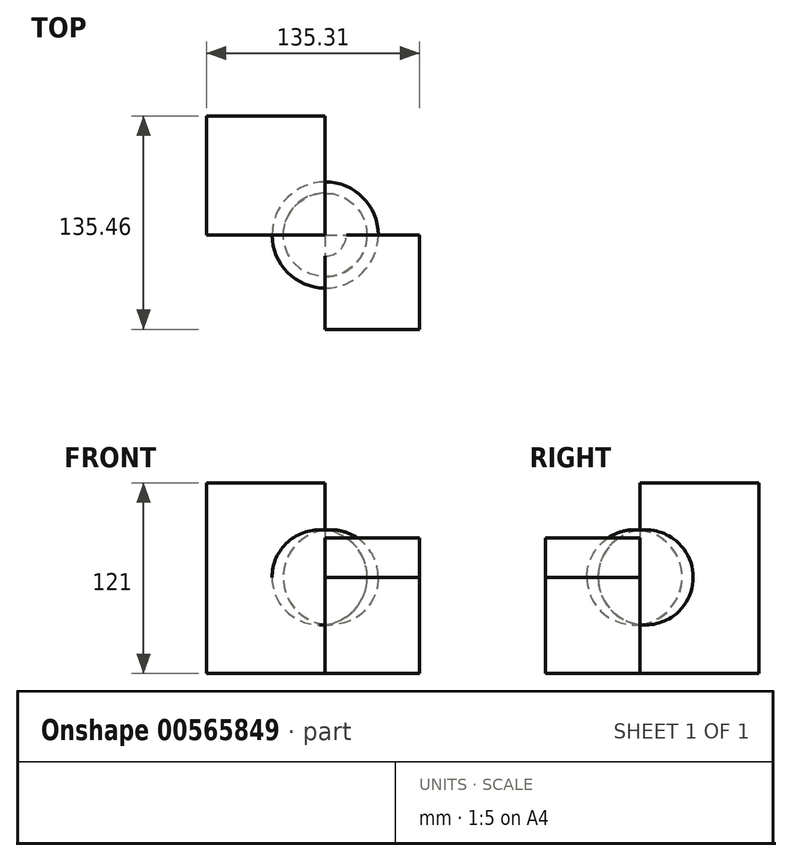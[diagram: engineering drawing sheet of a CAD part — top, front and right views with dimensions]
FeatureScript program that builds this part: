
annotation { "Feature Type Name" : "Feature", "Feature Type Description" : "" }
export const myFeature = defineFeature(function(context is Context, id is Id, definition is map)
    precondition{}
    {
        {
            var Q0;
            Q0=qCreatedBy(makeId("Front.planeOp"),FACE);
            var sketch = newSketch(context, id + "F0", { "sketchPlane" : qUnion([Q0])});
            skLineSegment(sketch, "E0", {"start": v(0, -30) * mm, "end": v(0, 30) * mm});
            skLineSegment(sketch, "E1", {"start": v(0, 0) * mm, "end": v(72.13, 0) * mm, "construction": true});
            skArc(sketch, "E2", {"start": v(0, 30) * mm, "mid": v(-26.67, 0) * mm, "end": v(0, -30) * mm});
            skSolve(sketch);
        }
        {
            var Q0;
            Q0=makeQuery(id+"F0.imprint","IMPRINT",FACE,{"disambiguationData":[TD([[makeQuery(id+"F0.imprint","IMPRINT",EDGE,{"derivedFrom":sQuery(id+"F0.wireOp",EDGE,"E0")}),1.0]])]});
            var Q1;
            Q1=sQuery(id+"F0.wireOp",EDGE,"E0");
            revolve(context, id + "F1", {"entities" : qUnion([Q0]), "axis" : qUnion([Q1]), "revolveType" : RevolveType.FULL});
        }
        {
            var Q0;
            Q0=qCreatedBy(makeId("Top.planeOp"),FACE);
            var sketch = newSketch(context, id + "F2", { "sketchPlane" : qUnion([Q0])});
            skLineSegment(sketch, "E3.bottom", {"start": v(0, 0) * mm, "end": v(60, 0) * mm});
            skLineSegment(sketch, "E3.top", {"start": v(0, -60) * mm, "end": v(60, -60) * mm});
            skLineSegment(sketch, "E3.right", {"start": v(60, 0) * mm, "end": v(60, -60) * mm});
            skLineSegment(sketch, "E4", {"start": v(0, 0) * mm, "end": v(0, -60) * mm});
            skPoint(sketch, "E3.left.end.orphan", {"position": v(-60, -60) * mm});
            skPoint(sketch, "E5.orphan", {"position": v(-60, 0) * mm});
            skLineSegment(sketch, "E6", {"start": v(0, 0) * mm, "end": v(0, 52.1) * mm, "construction": true});
            skSolve(sketch);
        }
        {
            var Q0;
            Q0 = qSketchRegion(id + "F2", true);
            extrude(context, id + "F3", {"entities" : qUnion([Q0]), "depth" : 25 * mm, "offsetDistance" : 25 * mm});
        }
        {
            var Q0;
            Q0=makeQuery(id+"F1.opRevolve","SWEPT_BODY",BODY,{"disambiguationData":[OSD([sQuery(id+"F0.wireOp",EDGE,"E0"),sQuery(id+"F0.wireOp",EDGE,"E2")])]});
            var Q1;
            Q1=makeQuery(id+"F3.opExtrude","SWEPT_BODY",BODY,{"disambiguationData":[OSD([sQuery(id+"F2.wireOp",EDGE,"E3.bottom"),sQuery(id+"F2.wireOp",EDGE,"E3.top"),sQuery(id+"F2.wireOp",EDGE,"E3.right"),sQuery(id+"F2.wireOp",EDGE,"E4")])]});
            booleanBodies(context, id + "F4", {"operationType" : BooleanOperationType.SUBTRACTION, "tools" : qUnion([Q0]), "targets" : qUnion([Q1]), "keepTools" : true});
        }
        {
            var Q0;
            Q0=makeQuery(id+"F3.opExtrude","CAP_FACE",FACE,{"disambiguationData":[OSD([sQuery(id+"F2.wireOp",EDGE,"E3.bottom"),sQuery(id+"F2.wireOp",EDGE,"E3.top"),sQuery(id+"F2.wireOp",EDGE,"E3.right"),sQuery(id+"F2.wireOp",EDGE,"E4")])],"isStart":true});
            var sketch = newSketch(context, id + "F5", { "sketchPlane" : qUnion([Q0])});
            skLineSegment(sketch, "E7.bottom", {"start": v(60, 60) * mm, "end": v(0, 60) * mm});
            skLineSegment(sketch, "E7.top", {"start": v(60, 0) * mm, "end": v(0, 0) * mm});
            skLineSegment(sketch, "E7.left", {"start": v(60, 60) * mm, "end": v(60, 0) * mm});
            skLineSegment(sketch, "E7.right", {"start": v(0, 60) * mm, "end": v(0, 0) * mm});
            skSolve(sketch);
        }
        {
            var Q0;
            Q0 = qSketchRegion(id + "F5", true);
            extrude(context, id + "F6", {"entities" : qUnion([Q0]), "depth" : 61 * mm, "offsetDistance" : 25 * mm});
        }
        {
            var Q0;
            Q0=makeQuery(id+"F6.opExtrude","CAP_FACE",FACE,{"disambiguationData":[OSD([sQuery(id+"F5.wireOp",EDGE,"E7.bottom"),sQuery(id+"F5.wireOp",EDGE,"E7.top"),sQuery(id+"F5.wireOp",EDGE,"E7.left"),sQuery(id+"F5.wireOp",EDGE,"E7.right")])],"isStart":false});
            var sketch = newSketch(context, id + "F7", { "sketchPlane" : qUnion([Q0])});
            skLineSegment(sketch, "E8.bottom", {"start": v(0, 0) * mm, "end": v(-75.3, 0) * mm});
            skLineSegment(sketch, "E8.top", {"start": v(0, -75.46) * mm, "end": v(-75.3, -75.46) * mm});
            skLineSegment(sketch, "E8.left", {"start": v(0, 0) * mm, "end": v(0, -75.46) * mm});
            skLineSegment(sketch, "E8.right", {"start": v(-75.3, 0) * mm, "end": v(-75.3, -75.46) * mm});
            skSolve(sketch);
        }
        {
            var Q0;
            Q0=makeQuery(id+"F7.imprint","IMPRINT",FACE,{"disambiguationData":[TD([[makeQuery(id+"F7.imprint","IMPRINT",EDGE,{"derivedFrom":sQuery(id+"F7.wireOp",EDGE,"E8.bottom")}),1.0]])]});
            extrude(context, id + "F8", {"entities" : qUnion([Q0]), "flatOperationType" : FlatOperationType.REMOVE, "oppositeDirection" : true, "depth" : 121 * mm, "offsetDistance" : 25 * mm, "domain" : OperationDomain.MODEL});
        }
        {
            var Q0;
            Q0=makeQuery(id+"F1.opRevolve","SWEPT_BODY",BODY,{"disambiguationData":[OSD([sQuery(id+"F0.wireOp",EDGE,"E0"),sQuery(id+"F0.wireOp",EDGE,"E2")])]});
            var Q1;
            Q1=makeQuery(id+"F8.opExtrude","SWEPT_BODY",BODY,{"disambiguationData":[OSD([sQuery(id+"F7.wireOp",EDGE,"E8.bottom"),sQuery(id+"F7.wireOp",EDGE,"E8.top"),sQuery(id+"F7.wireOp",EDGE,"E8.left"),sQuery(id+"F7.wireOp",EDGE,"E8.right")])]});
            booleanBodies(context, id + "F9", {"operationType" : BooleanOperationType.SUBTRACTION, "tools" : qUnion([Q0]), "targets" : qUnion([Q1]), "keepTools" : true});
        }
        {
            var Q0;
            Q0=makeQuery(id+"F1.opRevolve","SWEPT_BODY",BODY,{"disambiguationData":[OSD([sQuery(id+"F0.wireOp",EDGE,"E0"),sQuery(id+"F0.wireOp",EDGE,"E2")])]});
            var Q1;
            Q1=makeQuery(id+"F6.opExtrude","SWEPT_BODY",BODY,{"disambiguationData":[OSD([sQuery(id+"F5.wireOp",EDGE,"E7.bottom"),sQuery(id+"F5.wireOp",EDGE,"E7.top"),sQuery(id+"F5.wireOp",EDGE,"E7.left"),sQuery(id+"F5.wireOp",EDGE,"E7.right")])]});
            booleanBodies(context, id + "F10", {"operationType" : BooleanOperationType.SUBTRACTION, "tools" : qUnion([Q0]), "targets" : qUnion([Q1]), "keepTools" : true});
        }
    });
